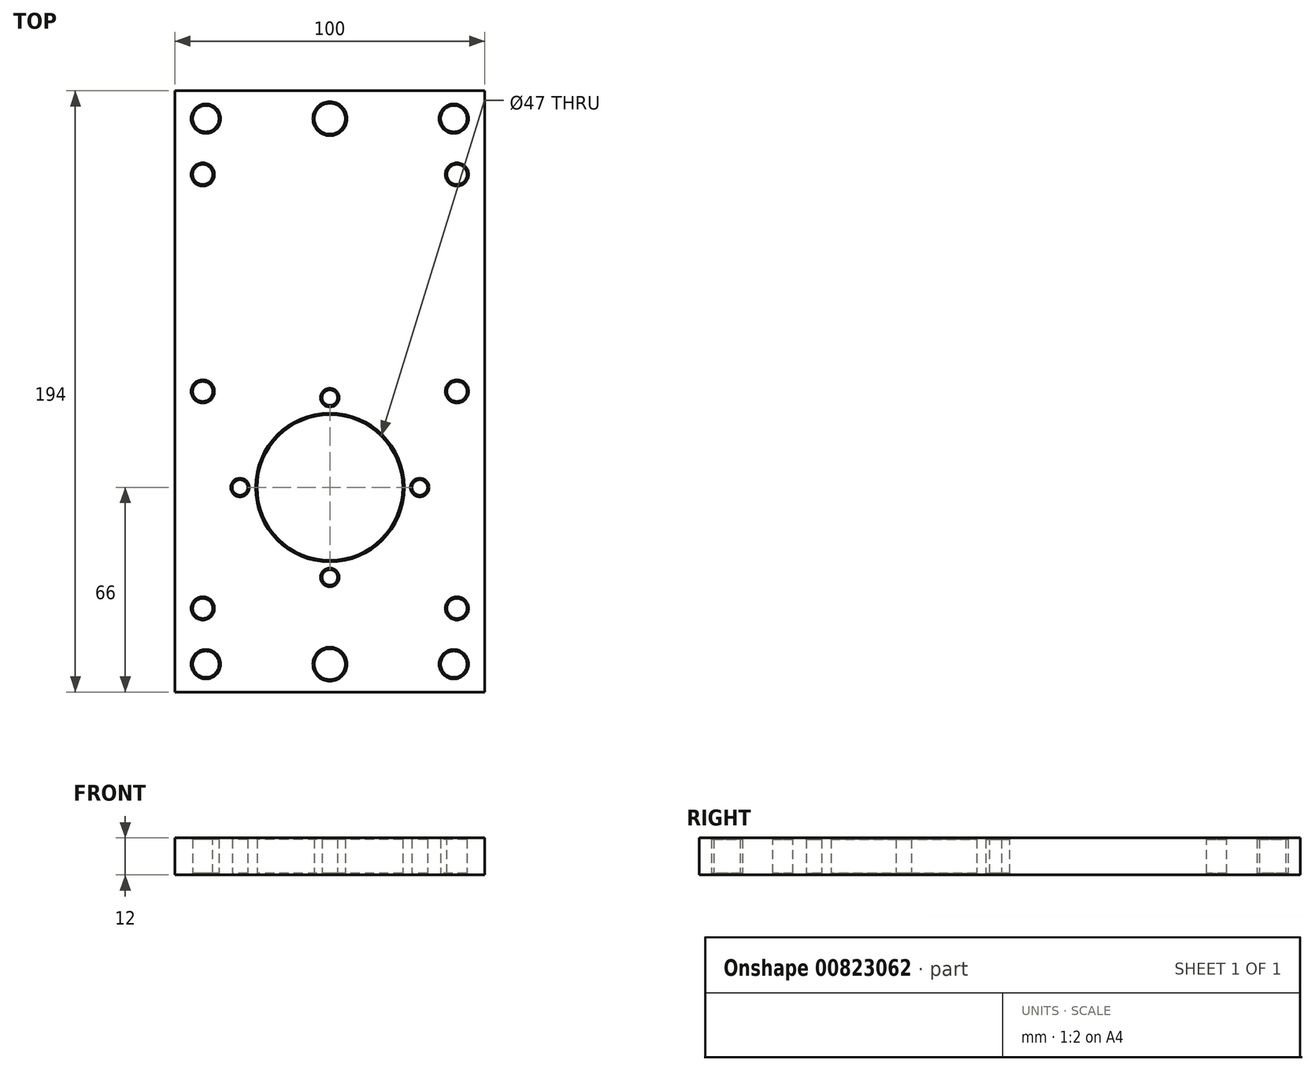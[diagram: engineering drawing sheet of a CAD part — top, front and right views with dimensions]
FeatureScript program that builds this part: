
annotation { "Feature Type Name" : "Feature", "Feature Type Description" : "" }
export const myFeature = defineFeature(function(context is Context, id is Id, definition is map)
    precondition{}
    {
        {
            var Q0;
            Q0=qCreatedBy(makeId("Top.planeOp"),FACE);
            var sketch = newSketch(context, id + "F0", { "sketchPlane" : qUnion([Q0])});
            skCircle(sketch, "E0", {"center": v(0, 0) * mm, "radius": 23.5 * mm});
            skLineSegment(sketch, "E1", {"start": v(0, 0) * mm, "end": v(0, 44.19) * mm, "construction": true});
            skLineSegment(sketch, "E2.bottom", {"start": v(50, -66) * mm, "end": v(-50, -66) * mm});
            skLineSegment(sketch, "E2.top", {"start": v(50, 128) * mm, "end": v(-50, 128) * mm});
            skLineSegment(sketch, "E2.left", {"start": v(50, -66) * mm, "end": v(50, 128) * mm});
            skLineSegment(sketch, "E2.right", {"start": v(-50, -66) * mm, "end": v(-50, 128) * mm});
            skPoint(sketch, "E2.middle", {"position": v(0, 31) * mm});
            skLineSegment(sketch, "E3", {"start": v(0, 0) * mm, "end": v(43.97, 0) * mm, "construction": true});
            skLineSegment(sketch, "E4", {"start": v(-50, 110) * mm, "end": v(50, 110) * mm, "construction": true});
            skLineSegment(sketch, "E5", {"start": v(-50, -48) * mm, "end": v(50, -48) * mm, "construction": true});
            skCircle(sketch, "E6", {"center": v(0, 0) * mm, "radius": 55 * mm, "construction": true});
            skCircle(sketch, "E7", {"center": v(0, 0) * mm, "radius": 65 * mm, "construction": true});
            skCircle(sketch, "E8", {"center": v(0, 0) * mm, "radius": 80 * mm, "construction": true});
            skLineSegment(sketch, "E9", {"start": v(0, 0) * mm, "end": v(-45.96, 45.96) * mm, "construction": true});
            skCircle(sketch, "E10", {"center": v(-45.96, 45.96) * mm, "radius": 5 * mm, "construction": true});
            skCircle(sketch, "E11.1.0", {"center": v(-45.96, -45.96) * mm, "radius": 5 * mm, "construction": true});
            skCircle(sketch, "E11.2.0", {"center": v(45.96, -45.96) * mm, "radius": 5 * mm, "construction": true});
            skCircle(sketch, "E11.3.0", {"center": v(45.96, 45.96) * mm, "radius": 5 * mm, "construction": true});
            skCircle(sketch, "E12", {"center": v(0, 0) * mm, "radius": 29 * mm, "construction": true});
            skCircle(sketch, "E13", {"center": v(0, 29) * mm, "radius": 2.5 * mm});
            skCircle(sketch, "E14.1.0", {"center": v(-29, 0) * mm, "radius": 2.5 * mm});
            skCircle(sketch, "E14.2.0", {"center": v(0, -29) * mm, "radius": 2.5 * mm});
            skCircle(sketch, "E14.3.0", {"center": v(29, 0) * mm, "radius": 2.5 * mm});
            skLineSegment(sketch, "E15.0", {"start": v(-50, 119) * mm, "end": v(50, 119) * mm, "construction": true});
            skLineSegment(sketch, "E16.0", {"start": v(-50, -57) * mm, "end": v(50, -57) * mm, "construction": true});
            skCircle(sketch, "E17", {"center": v(0, -57) * mm, "radius": 5 * mm});
            skCircle(sketch, "E18", {"center": v(0, 119) * mm, "radius": 5 * mm});
            skCircle(sketch, "E19", {"center": v(-40, 119) * mm, "radius": 4.25 * mm});
            skCircle(sketch, "E20.MirrorC", {"center": v(40, 119) * mm, "radius": 4.25 * mm});
            skLineSegment(sketch, "E21", {"start": v(50, 31) * mm, "end": v(98.03, 31) * mm, "construction": true});
            skCircle(sketch, "E22.MirrorC", {"center": v(40, -57) * mm, "radius": 4.25 * mm});
            skCircle(sketch, "E23.MirrorC", {"center": v(-40, -57) * mm, "radius": 4.25 * mm});
            skSolve(sketch);
        }
        {
            var Q0;
            Q0 = qSketchRegion(id + "F0", true);
            extrude(context, id + "F1", {"entities" : qUnion([Q0]), "depth" : 12 * mm, "offsetDistance" : 25 * mm});
        }
        {
            var Q0;
            Q0=makeQuery(id+"F1.opExtrude","SWEPT_FACE",FACE,{"disambiguationData":[OSD([sQuery(id+"F0.wireOp",EDGE,"E19")])]});
            var Q1;
            Q1=makeQuery(id+"F1.opExtrude","SWEPT_FACE",FACE,{"disambiguationData":[OSD([sQuery(id+"F0.wireOp",EDGE,"E18")])]});
            var Q2;
            Q2=makeQuery(id+"F1.opExtrude","SWEPT_FACE",FACE,{"disambiguationData":[OSD([sQuery(id+"F0.wireOp",EDGE,"E20.MirrorC")])]});
            var Q3;
            Q3=makeQuery(id+"F1.opExtrude","SWEPT_FACE",FACE,{"disambiguationData":[OSD([sQuery(id+"F0.wireOp",EDGE,"E0")])]});
            var Q4;
            Q4=makeQuery(id+"F1.opExtrude","SWEPT_FACE",FACE,{"disambiguationData":[OSD([sQuery(id+"F0.wireOp",EDGE,"E23.MirrorC")])]});
            var Q5;
            Q5=makeQuery(id+"F1.opExtrude","SWEPT_FACE",FACE,{"disambiguationData":[OSD([sQuery(id+"F0.wireOp",EDGE,"E17")])]});
            var Q6;
            Q6=makeQuery(id+"F1.opExtrude","SWEPT_FACE",FACE,{"disambiguationData":[OSD([sQuery(id+"F0.wireOp",EDGE,"E22.MirrorC")])]});
            var Q7;
            Q7=makeQuery(id+"F1.opExtrude","SWEPT_FACE",FACE,{"disambiguationData":[OSD([sQuery(id+"F0.wireOp",EDGE,"E13")])]});
            var Q8;
            Q8=makeQuery(id+"F1.opExtrude","SWEPT_FACE",FACE,{"disambiguationData":[OSD([sQuery(id+"F0.wireOp",EDGE,"E14.1.0")])]});
            var Q9;
            Q9=makeQuery(id+"F1.opExtrude","SWEPT_FACE",FACE,{"disambiguationData":[OSD([sQuery(id+"F0.wireOp",EDGE,"E14.2.0")])]});
            var Q10;
            Q10=makeQuery(id+"F1.opExtrude","SWEPT_FACE",FACE,{"disambiguationData":[OSD([sQuery(id+"F0.wireOp",EDGE,"E14.3.0")])]});
            chamfer(context, id + "F2", {"entities" : qUnion([Q0, Q1, Q2, Q3, Q4, Q5, Q6, Q7, Q8, Q9, Q10]), "width" : 0.5 * mm, "tangentPropagation" : true});
        }
        {
            var Q0;
            Q0=makeQuery(id+"F1.opExtrude","CAP_FACE",FACE,{"disambiguationData":[OSD([sQuery(id+"F0.wireOp",EDGE,"E0"),sQuery(id+"F0.wireOp",EDGE,"E2.bottom"),sQuery(id+"F0.wireOp",EDGE,"E2.top"),sQuery(id+"F0.wireOp",EDGE,"E2.left"),sQuery(id+"F0.wireOp",EDGE,"E2.right"),sQuery(id+"F0.wireOp",EDGE,"E13"),sQuery(id+"F0.wireOp",EDGE,"E14.1.0"),sQuery(id+"F0.wireOp",EDGE,"E14.2.0"),sQuery(id+"F0.wireOp",EDGE,"E14.3.0"),sQuery(id+"F0.wireOp",EDGE,"E17"),sQuery(id+"F0.wireOp",EDGE,"E18"),sQuery(id+"F0.wireOp",EDGE,"E19"),sQuery(id+"F0.wireOp",EDGE,"E20.MirrorC"),sQuery(id+"F0.wireOp",EDGE,"E22.MirrorC"),sQuery(id+"F0.wireOp",EDGE,"E23.MirrorC")])],"isStart":false});
            var sketch = newSketch(context, id + "F3", { "sketchPlane" : qUnion([Q0])});
            skLineSegment(sketch, "E24.0.0", {"start": v(50, -66) * mm, "end": v(50, 128) * mm, "construction": true});
            skLineSegment(sketch, "E24.0.1", {"start": v(50, 128) * mm, "end": v(-50, 128) * mm, "construction": true});
            skLineSegment(sketch, "E24.0.2", {"start": v(-50, 128) * mm, "end": v(-50, -66) * mm, "construction": true});
            skLineSegment(sketch, "E24.0.3", {"start": v(-50, -66) * mm, "end": v(50, -66) * mm, "construction": true});
            skLineSegment(sketch, "E25.0", {"start": v(41, -57) * mm, "end": v(41, 119) * mm, "construction": true});
            skLineSegment(sketch, "E25.1", {"start": v(-41, -57) * mm, "end": v(41, -57) * mm, "construction": true});
            skLineSegment(sketch, "E25.2", {"start": v(-41, 119) * mm, "end": v(-41, -57) * mm, "construction": true});
            skLineSegment(sketch, "E25.3", {"start": v(41, 119) * mm, "end": v(-41, 119) * mm, "construction": true});
            skLineSegment(sketch, "E26", {"start": v(-50, 31) * mm, "end": v(50, 31) * mm, "construction": true});
            skLineSegment(sketch, "E27", {"start": v(-50, 110) * mm, "end": v(50, 110) * mm, "construction": true});
            skLineSegment(sketch, "E28.0", {"start": v(-50, 101) * mm, "end": v(50, 101) * mm, "construction": true});
            skCircle(sketch, "E29", {"center": v(-41, 31) * mm, "radius": 3.25 * mm});
            skCircle(sketch, "E30", {"center": v(41, 31) * mm, "radius": 3.25 * mm});
            skCircle(sketch, "E31", {"center": v(41, 101) * mm, "radius": 3.25 * mm});
            skCircle(sketch, "E32", {"center": v(-41, 101) * mm, "radius": 3.25 * mm});
            skCircle(sketch, "E33.MirrorC", {"center": v(41, -39) * mm, "radius": 3.25 * mm});
            skCircle(sketch, "E34.MirrorC", {"center": v(-41, -39) * mm, "radius": 3.25 * mm});
            skSolve(sketch);
        }
        {
            var Q0;
            Q0 = qSketchRegion(id + "F3", true);
            extrude(context, id + "F4", {"entities" : qUnion([Q0]), "operationType" : NewBodyOperationType.REMOVE, "oppositeDirection" : true, "depth" : 25 * mm, "offsetDistance" : 25 * mm});
        }
        {
            var Q0;
            Q0=makeQuery(id+"F4.boolean.opBoolean","COPY",FACE,{"derivedFrom":makeQuery(id+"F4.opExtrude","SWEPT_FACE",FACE,{"disambiguationData":[OSD([sQuery(id+"F3.wireOp",EDGE,"E32")])]})});
            var Q1;
            Q1=makeQuery(id+"F4.boolean.opBoolean","COPY",FACE,{"derivedFrom":makeQuery(id+"F4.opExtrude","SWEPT_FACE",FACE,{"disambiguationData":[OSD([sQuery(id+"F3.wireOp",EDGE,"E31")])]})});
            var Q2;
            Q2=makeQuery(id+"F4.boolean.opBoolean","COPY",FACE,{"derivedFrom":makeQuery(id+"F4.opExtrude","SWEPT_FACE",FACE,{"disambiguationData":[OSD([sQuery(id+"F3.wireOp",EDGE,"E30")])]})});
            var Q3;
            Q3=makeQuery(id+"F4.boolean.opBoolean","COPY",FACE,{"derivedFrom":makeQuery(id+"F4.opExtrude","SWEPT_FACE",FACE,{"disambiguationData":[OSD([sQuery(id+"F3.wireOp",EDGE,"E29")])]})});
            var Q4;
            Q4=makeQuery(id+"F4.boolean.opBoolean","COPY",FACE,{"derivedFrom":makeQuery(id+"F4.opExtrude","SWEPT_FACE",FACE,{"disambiguationData":[OSD([sQuery(id+"F3.wireOp",EDGE,"E34.MirrorC")])]})});
            var Q5;
            Q5=makeQuery(id+"F4.boolean.opBoolean","COPY",FACE,{"derivedFrom":makeQuery(id+"F4.opExtrude","SWEPT_FACE",FACE,{"disambiguationData":[OSD([sQuery(id+"F3.wireOp",EDGE,"E33.MirrorC")])]})});
            chamfer(context, id + "F5", {"entities" : qUnion([Q0, Q1, Q2, Q3, Q4, Q5]), "width" : 0.5 * mm, "tangentPropagation" : true});
        }
    });
